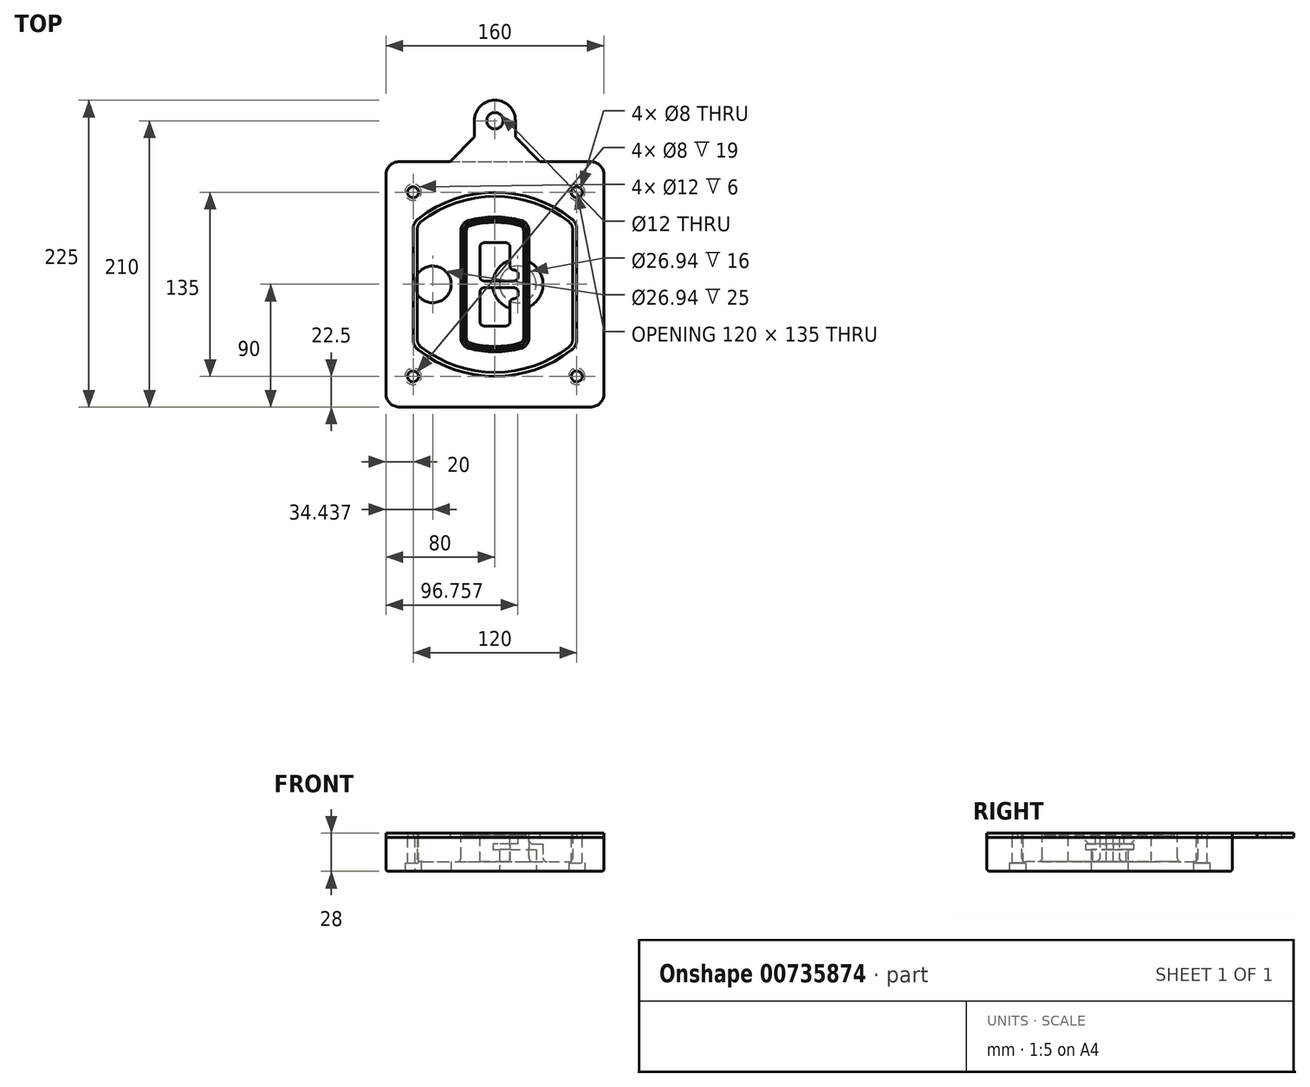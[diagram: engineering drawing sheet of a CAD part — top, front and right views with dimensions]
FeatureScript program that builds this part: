
annotation { "Feature Type Name" : "Feature", "Feature Type Description" : "" }
export const myFeature = defineFeature(function(context is Context, id is Id, definition is map)
    precondition{}
    {
        {
            var Q0;
            Q0=qCreatedBy(makeId("Top.planeOp"),FACE);
            var sketch = newSketch(context, id + "F0", { "sketchPlane" : qUnion([Q0])});
            skPoint(sketch, "E0.rect.middle", {"position": v(0, 0) * mm});
            skLineSegment(sketch, "E1.bottom", {"start": v(-70, -90) * mm, "end": v(70, -90) * mm});
            skLineSegment(sketch, "E1.top", {"start": v(-70, 90) * mm, "end": v(70, 90) * mm});
            skLineSegment(sketch, "E1.left", {"start": v(-80, -80) * mm, "end": v(-80, 80) * mm});
            skLineSegment(sketch, "E1.right", {"start": v(80, -80) * mm, "end": v(80, 80) * mm});
            skLineSegment(sketch, "E2", {"start": v(-80, 90) * mm, "end": v(80, -90) * mm, "construction": true});
            skLineSegment(sketch, "E3", {"start": v(80, 90) * mm, "end": v(-80, -90) * mm, "construction": true});
            skCircle(sketch, "E4", {"center": v(-60, 67.5) * mm, "radius": 4 * mm});
            skCircle(sketch, "E5", {"center": v(60, 67.5) * mm, "radius": 4 * mm});
            skCircle(sketch, "E6", {"center": v(60, -67.5) * mm, "radius": 4 * mm});
            skCircle(sketch, "E7", {"center": v(-60, -67.5) * mm, "radius": 4 * mm});
            skLineSegment(sketch, "E8", {"start": v(-60, 67.5) * mm, "end": v(60, 67.5) * mm, "construction": true});
            skLineSegment(sketch, "E9", {"start": v(60, 67.5) * mm, "end": v(60, -67.5) * mm, "construction": true});
            skLineSegment(sketch, "E10", {"start": v(60, -67.5) * mm, "end": v(-60, -67.5) * mm, "construction": true});
            skLineSegment(sketch, "E11", {"start": v(-60, -67.5) * mm, "end": v(-60, 67.5) * mm, "construction": true});
            skLineSegment(sketch, "E12", {"start": v(-60, 40.3) * mm, "end": v(-60, -40.3) * mm});
            skLineSegment(sketch, "E13", {"start": v(60, 40.3) * mm, "end": v(60, -40.3) * mm});
            skArc(sketch, "E14", {"start": v(56.15, 48.18) * mm, "mid": v(0, 67.5) * mm, "end": v(-56.15, 48.18) * mm});
            skArc(sketch, "E15", {"start": v(-56.15, -48.18) * mm, "mid": v(0, -67.5) * mm, "end": v(56.15, -48.18) * mm});
            skLineSegment(sketch, "E16", {"start": v(-60, 0) * mm, "end": v(60, 0) * mm, "construction": true});
            skPoint(sketch, "E17.visualSharp", {"position": v(-60, -45) * mm});
            skArc(sketch, "E17.filletArc", {"start": v(-60, -40.3) * mm, "mid": v(-58.99, -44.68) * mm, "end": v(-56.15, -48.18) * mm});
            skPoint(sketch, "E18.visualSharp", {"position": v(-60, 45) * mm});
            skArc(sketch, "E18.filletArc", {"start": v(-56.15, 48.18) * mm, "mid": v(-58.99, 44.68) * mm, "end": v(-60, 40.3) * mm});
            skPoint(sketch, "E19.visualSharp", {"position": v(60, 45) * mm});
            skArc(sketch, "E19.filletArc", {"start": v(60, 40.3) * mm, "mid": v(58.99, 44.68) * mm, "end": v(56.15, 48.18) * mm});
            skPoint(sketch, "E20.visualSharp", {"position": v(60, -45) * mm});
            skArc(sketch, "E20.filletArc", {"start": v(56.15, -48.18) * mm, "mid": v(58.99, -44.68) * mm, "end": v(60, -40.3) * mm});
            skPoint(sketch, "E21.visualSharp", {"position": v(-80, 90) * mm});
            skArc(sketch, "E21.filletArc", {"start": v(-70, 90) * mm, "mid": v(-77.07, 87.07) * mm, "end": v(-80, 80) * mm});
            skPoint(sketch, "E22.visualSharp", {"position": v(80, 90) * mm});
            skArc(sketch, "E22.filletArc", {"start": v(80, 80) * mm, "mid": v(77.07, 87.07) * mm, "end": v(70, 90) * mm});
            skPoint(sketch, "E23.visualSharp", {"position": v(80, -90) * mm});
            skArc(sketch, "E23.filletArc", {"start": v(70, -90) * mm, "mid": v(77.07, -87.07) * mm, "end": v(80, -80) * mm});
            skPoint(sketch, "E24.visualSharp", {"position": v(-80, -90) * mm});
            skArc(sketch, "E24.filletArc", {"start": v(-80, -80) * mm, "mid": v(-77.07, -87.07) * mm, "end": v(-70, -90) * mm});
            skArc(sketch, "E25.0", {"start": v(57, 40.3) * mm, "mid": v(56.3, 43.36) * mm, "end": v(54.3, 45.81) * mm});
            skLineSegment(sketch, "E25.1", {"start": v(57, 40.3) * mm, "end": v(57, -40.3) * mm});
            skArc(sketch, "E25.2", {"start": v(54.3, -45.81) * mm, "mid": v(56.3, -43.36) * mm, "end": v(57, -40.3) * mm});
            skArc(sketch, "E25.3", {"start": v(-54.3, -45.81) * mm, "mid": v(0, -64.5) * mm, "end": v(54.3, -45.81) * mm});
            skArc(sketch, "E25.4", {"start": v(-57, -40.3) * mm, "mid": v(-56.3, -43.36) * mm, "end": v(-54.3, -45.81) * mm});
            skArc(sketch, "E25.5", {"start": v(54.3, 45.81) * mm, "mid": v(0, 64.5) * mm, "end": v(-54.3, 45.81) * mm});
            skLineSegment(sketch, "E25.6", {"start": v(-57, 40.3) * mm, "end": v(-57, -40.3) * mm});
            skArc(sketch, "E25.7", {"start": v(-54.3, 45.81) * mm, "mid": v(-56.3, 43.36) * mm, "end": v(-57, 40.3) * mm});
            skArc(sketch, "E26.0", {"start": v(-58.62, 51.33) * mm, "mid": v(-62.58, 46.43) * mm, "end": v(-64, 40.3) * mm});
            skArc(sketch, "E26.1", {"start": v(58.62, 51.33) * mm, "mid": v(0, 71.5) * mm, "end": v(-58.62, 51.33) * mm});
            skArc(sketch, "E26.2", {"start": v(64, 40.3) * mm, "mid": v(62.58, 46.43) * mm, "end": v(58.62, 51.33) * mm});
            skLineSegment(sketch, "E26.3", {"start": v(64, 40.3) * mm, "end": v(64, -40.3) * mm});
            skArc(sketch, "E26.4", {"start": v(58.62, -51.33) * mm, "mid": v(62.58, -46.43) * mm, "end": v(64, -40.3) * mm});
            skLineSegment(sketch, "E26.5", {"start": v(-64, 40.3) * mm, "end": v(-64, -40.3) * mm});
            skArc(sketch, "E26.6", {"start": v(-58.62, -51.33) * mm, "mid": v(0, -71.5) * mm, "end": v(58.62, -51.33) * mm});
            skArc(sketch, "E26.7", {"start": v(-64, -40.3) * mm, "mid": v(-62.58, -46.43) * mm, "end": v(-58.62, -51.33) * mm});
            skSolve(sketch);
        }
        {
            var Q0;
            Q0=makeQuery(id+"F0.imprint","IMPRINT",FACE,{"disambiguationData":[TD([[makeQuery(id+"F0.imprint","IMPRINT",EDGE,{"derivedFrom":sQuery(id+"F0.wireOp",EDGE,"E1.bottom")}),1.0]])]});
            var Q1;
            Q1=makeQuery(id+"F0.imprint","IMPRINT",FACE,{"disambiguationData":[TD([[makeQuery(id+"F0.imprint","IMPRINT",EDGE,{"derivedFrom":sQuery(id+"F0.wireOp",EDGE,"E12")}),1.0]])]});
            var Q2;
            Q2=makeQuery(id+"F0.imprint","IMPRINT",FACE,{"disambiguationData":[TD([[makeQuery(id+"F0.imprint","IMPRINT",EDGE,{"derivedFrom":sQuery(id+"F0.wireOp",EDGE,"E25.0")}),1.0]])]});
            var Q3;
            Q3=makeQuery(id+"F0.imprint","IMPRINT",FACE,{"disambiguationData":[TD([[makeQuery(id+"F0.imprint","IMPRINT",EDGE,{"derivedFrom":sQuery(id+"F0.wireOp",EDGE,"E12")}),-1.0]])]});
            extrude(context, id + "F1", {"entities" : qUnion([Q0, Q1, Q2, Q3]), "oppositeDirection" : true, "depth" : 25 * mm});
        }
        {
            var Q0;
            Q0=makeQuery(id+"F0.imprint","IMPRINT",FACE,{"disambiguationData":[TD([[makeQuery(id+"F0.imprint","IMPRINT",EDGE,{"derivedFrom":sQuery(id+"F0.wireOp",EDGE,"E12")}),1.0]])]});
            extrude(context, id + "F2", {"entities" : qUnion([Q0]), "operationType" : NewBodyOperationType.ADD, "depth" : 3 * mm});
        }
        {
            var Q0;
            Q0=makeQuery(id+"F0.imprint","IMPRINT",FACE,{"disambiguationData":[TD([[makeQuery(id+"F0.imprint","IMPRINT",EDGE,{"derivedFrom":sQuery(id+"F0.wireOp",EDGE,"E25.0")}),1.0]])]});
            extrude(context, id + "F3", {"entities" : qUnion([Q0]), "operationType" : NewBodyOperationType.REMOVE, "oppositeDirection" : true, "depth" : 18 * mm});
        }
        {
            var Q0;
            Q0=makeQuery(id+"F2.opExtrude","CAP_FACE",FACE,{"disambiguationData":[OSD([sQuery(id+"F0.wireOp",EDGE,"E12"),sQuery(id+"F0.wireOp",EDGE,"E13"),sQuery(id+"F0.wireOp",EDGE,"E14"),sQuery(id+"F0.wireOp",EDGE,"E15"),sQuery(id+"F0.wireOp",EDGE,"E17.filletArc"),sQuery(id+"F0.wireOp",EDGE,"E18.filletArc"),sQuery(id+"F0.wireOp",EDGE,"E19.filletArc"),sQuery(id+"F0.wireOp",EDGE,"E20.filletArc"),sQuery(id+"F0.wireOp",EDGE,"E25.0"),sQuery(id+"F0.wireOp",EDGE,"E25.1"),sQuery(id+"F0.wireOp",EDGE,"E25.2"),sQuery(id+"F0.wireOp",EDGE,"E25.3"),sQuery(id+"F0.wireOp",EDGE,"E25.4"),sQuery(id+"F0.wireOp",EDGE,"E25.5"),sQuery(id+"F0.wireOp",EDGE,"E25.6"),sQuery(id+"F0.wireOp",EDGE,"E25.7")])],"isStart":false});
            var sketch = newSketch(context, id + "F4", { "sketchPlane" : qUnion([Q0])});
            skArc(sketch, "E27.0", {"start": v(-19.08, -46.97) * mm, "mid": v(0, -49.5) * mm, "end": v(19.08, -46.97) * mm});
            skArc(sketch, "E28.0", {"start": v(19.08, 46.97) * mm, "mid": v(0, 49.5) * mm, "end": v(-19.08, 46.97) * mm});
            skLineSegment(sketch, "E29", {"start": v(-25, 39.25) * mm, "end": v(-25, -39.25) * mm});
            skLineSegment(sketch, "E30", {"start": v(25, 39.25) * mm, "end": v(25, -39.25) * mm});
            skLineSegment(sketch, "E31", {"start": v(-25, 45.1) * mm, "end": v(25, 45.1) * mm, "construction": true});
            skLineSegment(sketch, "E32", {"start": v(-25, -45.1) * mm, "end": v(25, -45.1) * mm, "construction": true});
            skPoint(sketch, "E33.visualSharp", {"position": v(-25, 45.1) * mm});
            skArc(sketch, "E33.filletArc", {"start": v(-19.08, 46.97) * mm, "mid": v(-23.35, 44.11) * mm, "end": v(-25, 39.25) * mm});
            skPoint(sketch, "E34.visualSharp", {"position": v(25, 45.1) * mm});
            skArc(sketch, "E34.filletArc", {"start": v(25, 39.25) * mm, "mid": v(23.35, 44.11) * mm, "end": v(19.08, 46.97) * mm});
            skPoint(sketch, "E35.visualSharp", {"position": v(25, -45.1) * mm});
            skArc(sketch, "E35.filletArc", {"start": v(19.08, -46.97) * mm, "mid": v(23.35, -44.11) * mm, "end": v(25, -39.25) * mm});
            skPoint(sketch, "E36.visualSharp", {"position": v(-25, -45.1) * mm});
            skArc(sketch, "E36.filletArc", {"start": v(-25, -39.25) * mm, "mid": v(-23.35, -44.11) * mm, "end": v(-19.08, -46.97) * mm});
            skArc(sketch, "E37.0", {"start": v(54.3, 45.81) * mm, "mid": v(0, 64.5) * mm, "end": v(-54.3, 45.81) * mm});
            skArc(sketch, "E37.1", {"start": v(-54.3, 45.81) * mm, "mid": v(-56.3, 43.36) * mm, "end": v(-57, 40.3) * mm});
            skLineSegment(sketch, "E37.2", {"start": v(-57, 40.3) * mm, "end": v(-57, -40.3) * mm});
            skArc(sketch, "E37.3", {"start": v(-57, -40.3) * mm, "mid": v(-56.3, -43.36) * mm, "end": v(-54.3, -45.81) * mm});
            skArc(sketch, "E37.4", {"start": v(-54.3, -45.81) * mm, "mid": v(0, -64.5) * mm, "end": v(54.3, -45.81) * mm});
            skArc(sketch, "E37.5", {"start": v(54.3, -45.81) * mm, "mid": v(56.3, -43.36) * mm, "end": v(57, -40.3) * mm});
            skLineSegment(sketch, "E37.6", {"start": v(57, 40.3) * mm, "end": v(57, -40.3) * mm});
            skArc(sketch, "E37.7", {"start": v(57, 40.3) * mm, "mid": v(56.3, 43.36) * mm, "end": v(54.3, 45.81) * mm});
            skLineSegment(sketch, "E38.0", {"start": v(23, 39.25) * mm, "end": v(23, -39.25) * mm});
            skArc(sketch, "E38.1", {"start": v(18.56, -45.04) * mm, "mid": v(21.76, -42.9) * mm, "end": v(23, -39.25) * mm});
            skArc(sketch, "E38.2", {"start": v(-18.56, -45.04) * mm, "mid": v(0, -47.5) * mm, "end": v(18.56, -45.04) * mm});
            skArc(sketch, "E38.3", {"start": v(-23, -39.25) * mm, "mid": v(-21.76, -42.9) * mm, "end": v(-18.56, -45.04) * mm});
            skLineSegment(sketch, "E38.4", {"start": v(-23, 39.25) * mm, "end": v(-23, -39.25) * mm});
            skArc(sketch, "E38.5", {"start": v(23, 39.25) * mm, "mid": v(21.76, 42.9) * mm, "end": v(18.56, 45.04) * mm});
            skArc(sketch, "E38.6", {"start": v(-18.56, 45.04) * mm, "mid": v(-21.76, 42.9) * mm, "end": v(-23, 39.25) * mm});
            skArc(sketch, "E38.7", {"start": v(18.56, 45.04) * mm, "mid": v(0, 47.5) * mm, "end": v(-18.56, 45.04) * mm});
            skArc(sketch, "E39.0", {"start": v(21, 39.25) * mm, "mid": v(20.18, 41.68) * mm, "end": v(18.04, 43.1) * mm});
            skLineSegment(sketch, "E39.1", {"start": v(21, 39.25) * mm, "end": v(21, -39.25) * mm});
            skArc(sketch, "E39.2", {"start": v(18.04, -43.1) * mm, "mid": v(20.18, -41.68) * mm, "end": v(21, -39.25) * mm});
            skArc(sketch, "E39.3", {"start": v(-18.04, -43.1) * mm, "mid": v(0, -45.5) * mm, "end": v(18.04, -43.1) * mm});
            skArc(sketch, "E39.4", {"start": v(-21, -39.25) * mm, "mid": v(-20.18, -41.68) * mm, "end": v(-18.04, -43.1) * mm});
            skArc(sketch, "E39.5", {"start": v(18.04, 43.1) * mm, "mid": v(0, 45.5) * mm, "end": v(-18.04, 43.1) * mm});
            skLineSegment(sketch, "E39.6", {"start": v(-21, 39.25) * mm, "end": v(-21, -39.25) * mm});
            skArc(sketch, "E39.7", {"start": v(-18.04, 43.1) * mm, "mid": v(-20.18, 41.68) * mm, "end": v(-21, 39.25) * mm});
            skLineSegment(sketch, "E40", {"start": v(-25, 0) * mm, "end": v(25, 0) * mm, "construction": true});
            skLineSegment(sketch, "E41", {"start": v(-11, 5.5) * mm, "end": v(-11, 27.5) * mm});
            skLineSegment(sketch, "E42", {"start": v(-8, 30.5) * mm, "end": v(8, 30.5) * mm});
            skLineSegment(sketch, "E43", {"start": v(11, 27.5) * mm, "end": v(11, 13.5) * mm});
            skLineSegment(sketch, "E44", {"start": v(14, 10.5) * mm, "end": v(14, 10.5) * mm});
            skLineSegment(sketch, "E45", {"start": v(17, 7.5) * mm, "end": v(17, 5.5) * mm});
            skLineSegment(sketch, "E46", {"start": v(14, 2.5) * mm, "end": v(-8, 2.5) * mm});
            skPoint(sketch, "E47.visualSharp", {"position": v(-11, 30.5) * mm});
            skArc(sketch, "E47.filletArc", {"start": v(-8, 30.5) * mm, "mid": v(-10.12, 29.62) * mm, "end": v(-11, 27.5) * mm});
            skPoint(sketch, "E48.visualSharp", {"position": v(11, 30.5) * mm});
            skArc(sketch, "E48.filletArc", {"start": v(11, 27.5) * mm, "mid": v(10.12, 29.62) * mm, "end": v(8, 30.5) * mm});
            skPoint(sketch, "E49.visualSharp", {"position": v(11, 10.5) * mm});
            skArc(sketch, "E49.filletArc", {"start": v(11, 13.5) * mm, "mid": v(11.88, 11.38) * mm, "end": v(14, 10.5) * mm});
            skPoint(sketch, "E50.visualSharp", {"position": v(17, 10.5) * mm});
            skArc(sketch, "E50.filletArc", {"start": v(17, 7.5) * mm, "mid": v(16.12, 9.62) * mm, "end": v(14, 10.5) * mm});
            skPoint(sketch, "E51.visualSharp", {"position": v(17, 2.5) * mm});
            skArc(sketch, "E51.filletArc", {"start": v(14, 2.5) * mm, "mid": v(16.12, 3.38) * mm, "end": v(17, 5.5) * mm});
            skPoint(sketch, "E52.visualSharp", {"position": v(-11, 2.5) * mm});
            skArc(sketch, "E52.filletArc", {"start": v(-11, 5.5) * mm, "mid": v(-10.12, 3.38) * mm, "end": v(-8, 2.5) * mm});
            skLineSegment(sketch, "E53.0.MirrorCS", {"start": v(14, -2.5) * mm, "end": v(-8, -2.5) * mm});
            skArc(sketch, "E54.0.MirrorCS", {"start": v(-11, -5.5) * mm, "mid": v(-10.12, -3.38) * mm, "end": v(-8, -2.5) * mm});
            skLineSegment(sketch, "E55.0.MirrorCS", {"start": v(-11, -5.5) * mm, "end": v(-11, -27.5) * mm});
            skArc(sketch, "E56.0.MirrorCS", {"start": v(-8, -30.5) * mm, "mid": v(-10.12, -29.62) * mm, "end": v(-11, -27.5) * mm});
            skLineSegment(sketch, "E57.0.MirrorCS", {"start": v(-8, -30.5) * mm, "end": v(8, -30.5) * mm});
            skArc(sketch, "E58.0.MirrorCS", {"start": v(11, -27.5) * mm, "mid": v(10.12, -29.62) * mm, "end": v(8, -30.5) * mm});
            skLineSegment(sketch, "E59.0.MirrorCS", {"start": v(11, -27.5) * mm, "end": v(11, -13.5) * mm});
            skArc(sketch, "E60.0.MirrorCS", {"start": v(11, -13.5) * mm, "mid": v(11.88, -11.38) * mm, "end": v(14, -10.5) * mm});
            skArc(sketch, "E61.0.MirrorCS", {"start": v(17, -7.5) * mm, "mid": v(16.12, -9.62) * mm, "end": v(14, -10.5) * mm});
            skLineSegment(sketch, "E62.0.MirrorCS", {"start": v(17, -7.5) * mm, "end": v(17, -5.5) * mm});
            skArc(sketch, "E63.0.MirrorCS", {"start": v(14, -2.5) * mm, "mid": v(16.12, -3.38) * mm, "end": v(17, -5.5) * mm});
            skSolve(sketch);
        }
        {
            var Q0;
            Q0=makeQuery(id+"F4.imprint","IMPRINT",FACE,{"disambiguationData":[TD([[makeQuery(id+"F4.imprint","IMPRINT",EDGE,{"derivedFrom":sQuery(id+"F4.wireOp",EDGE,"E27.0")}),1.0]])]});
            var Q1;
            Q1=makeQuery(id+"F4.imprint","IMPRINT",FACE,{"disambiguationData":[TD([[makeQuery(id+"F4.imprint","IMPRINT",EDGE,{"derivedFrom":sQuery(id+"F4.wireOp",EDGE,"E38.0")}),-1.0]])]});
            var Q2;
            Q2=makeQuery(id+"F4.imprint","IMPRINT",FACE,{"disambiguationData":[TD([[makeQuery(id+"F4.imprint","IMPRINT",EDGE,{"derivedFrom":sQuery(id+"F4.wireOp",EDGE,"E39.0")}),1.0]])]});
            extrude(context, id + "F5", {"entities" : qUnion([Q0, Q1, Q2]), "operationType" : NewBodyOperationType.ADD, "endBound" : BoundingType.UP_TO_NEXT, "oppositeDirection" : true, "depth" : 25 * mm});
        }
        {
            var Q0;
            Q0=makeQuery(id+"F4.imprint","IMPRINT",FACE,{"disambiguationData":[TD([[makeQuery(id+"F4.imprint","IMPRINT",EDGE,{"derivedFrom":sQuery(id+"F4.wireOp",EDGE,"E38.0")}),-1.0]])]});
            extrude(context, id + "F6", {"entities" : qUnion([Q0]), "operationType" : NewBodyOperationType.REMOVE, "oppositeDirection" : true, "depth" : 2 * mm});
        }
        {
            var Q0;
            Q0=makeQuery(id+"F1.opExtrude","CAP_FACE",FACE,{"disambiguationData":[OSD([sQuery(id+"F0.wireOp",EDGE,"E1.bottom"),sQuery(id+"F0.wireOp",EDGE,"E1.top"),sQuery(id+"F0.wireOp",EDGE,"E1.left"),sQuery(id+"F0.wireOp",EDGE,"E1.right"),sQuery(id+"F0.wireOp",EDGE,"E4"),sQuery(id+"F0.wireOp",EDGE,"E5"),sQuery(id+"F0.wireOp",EDGE,"E6"),sQuery(id+"F0.wireOp",EDGE,"E7"),sQuery(id+"F0.wireOp",EDGE,"E21.filletArc"),sQuery(id+"F0.wireOp",EDGE,"E22.filletArc"),sQuery(id+"F0.wireOp",EDGE,"E23.filletArc"),sQuery(id+"F0.wireOp",EDGE,"E24.filletArc")])],"isStart":false});
            var sketch = newSketch(context, id + "F7", { "sketchPlane" : qUnion([Q0])});
            skCircle(sketch, "E64", {"center": v(16.76, 0) * mm, "radius": 13.47 * mm});
            skCircle(sketch, "E65", {"center": v(-45.56, 0) * mm, "radius": 13.47 * mm});
            skLineSegment(sketch, "E66", {"start": v(80, 0) * mm, "end": v(-80, 0) * mm});
            skCircle(sketch, "E67", {"center": v(16.76, 0) * mm, "radius": 18.47 * mm});
            skCircle(sketch, "E68", {"center": v(60, -67.5) * mm, "radius": 6 * mm});
            skCircle(sketch, "E69", {"center": v(-60, -67.5) * mm, "radius": 6 * mm});
            skCircle(sketch, "E70", {"center": v(-60, 67.5) * mm, "radius": 6 * mm});
            skCircle(sketch, "E71", {"center": v(60, 67.5) * mm, "radius": 6 * mm});
            skSolve(sketch);
        }
        {
            var Q0;
            {var subQ1=sQuery(id+"F7.wireOp",EDGE,"E66");var subQ4=sQuery(id+"F7.wireOp",EDGE,"E64");var subQ6=makeQuery(id+"F7.imprint","INTERSECT",VERTEX,{"disambiguationData":[OD(0.0)],"derivedFrom":[subQ4,subQ1]});Q0=makeQuery(id+"F7.imprint","IMPRINT",FACE,{"disambiguationData":[TD([[makeQuery(id+"F7.imprint","IMPRINT",EDGE,{"disambiguationData":[TD([[subQ6,-1.0]])],"derivedFrom":subQ4}),-1.0]])]});}
            var Q1;
            {var subQ0=sQuery(id+"F7.wireOp",EDGE,"E66");var subQ1=sQuery(id+"F7.wireOp",EDGE,"E64");var subQ3=makeQuery(id+"F7.imprint","INTERSECT",VERTEX,{"disambiguationData":[OD(0.0)],"derivedFrom":[subQ1,subQ0]});Q1=makeQuery(id+"F7.imprint","IMPRINT",FACE,{"disambiguationData":[TD([[makeQuery(id+"F7.imprint","IMPRINT",EDGE,{"disambiguationData":[TD([[subQ3,-1.0]])],"derivedFrom":subQ1}),1.0]])]});}
            var Q2;
            {var subQ0=sQuery(id+"F7.wireOp",EDGE,"E66");var subQ1=sQuery(id+"F7.wireOp",EDGE,"E64");var subQ3=makeQuery(id+"F7.imprint","INTERSECT",VERTEX,{"disambiguationData":[OD(0.0)],"derivedFrom":[subQ1,subQ0]});Q2=makeQuery(id+"F7.imprint","IMPRINT",FACE,{"disambiguationData":[TD([[makeQuery(id+"F7.imprint","IMPRINT",EDGE,{"disambiguationData":[TD([[subQ3,1.0]])],"derivedFrom":subQ1}),1.0]])]});}
            var Q3;
            {var subQ1=sQuery(id+"F7.wireOp",EDGE,"E66");var subQ4=sQuery(id+"F7.wireOp",EDGE,"E64");var subQ6=makeQuery(id+"F7.imprint","INTERSECT",VERTEX,{"disambiguationData":[OD(0.0)],"derivedFrom":[subQ4,subQ1]});Q3=makeQuery(id+"F7.imprint","IMPRINT",FACE,{"disambiguationData":[TD([[makeQuery(id+"F7.imprint","IMPRINT",EDGE,{"disambiguationData":[TD([[subQ6,1.0]])],"derivedFrom":subQ4}),-1.0]])]});}
            extrude(context, id + "F8", {"entities" : qUnion([Q0, Q1, Q2, Q3]), "operationType" : NewBodyOperationType.ADD, "oppositeDirection" : true, "depth" : 20 * mm});
        }
        {
            var Q0;
            {var subQ0=sQuery(id+"F7.wireOp",EDGE,"E66");var subQ1=sQuery(id+"F7.wireOp",EDGE,"E64");var subQ3=makeQuery(id+"F7.imprint","INTERSECT",VERTEX,{"disambiguationData":[OD(0.0)],"derivedFrom":[subQ1,subQ0]});Q0=makeQuery(id+"F7.imprint","IMPRINT",FACE,{"disambiguationData":[TD([[makeQuery(id+"F7.imprint","IMPRINT",EDGE,{"disambiguationData":[TD([[subQ3,-1.0]])],"derivedFrom":subQ1}),1.0]])]});}
            var Q1;
            {var subQ0=sQuery(id+"F7.wireOp",EDGE,"E66");var subQ1=sQuery(id+"F7.wireOp",EDGE,"E64");var subQ3=makeQuery(id+"F7.imprint","INTERSECT",VERTEX,{"disambiguationData":[OD(0.0)],"derivedFrom":[subQ1,subQ0]});Q1=makeQuery(id+"F7.imprint","IMPRINT",FACE,{"disambiguationData":[TD([[makeQuery(id+"F7.imprint","IMPRINT",EDGE,{"disambiguationData":[TD([[subQ3,1.0]])],"derivedFrom":subQ1}),1.0]])]});}
            extrude(context, id + "F9", {"entities" : qUnion([Q0, Q1]), "operationType" : NewBodyOperationType.REMOVE, "oppositeDirection" : true, "depth" : 16 * mm});
        }
        {
            var Q0;
            {var subQ0=sQuery(id+"F7.wireOp",EDGE,"E66");var subQ1=sQuery(id+"F7.wireOp",EDGE,"E65");var subQ3=makeQuery(id+"F7.imprint","INTERSECT",VERTEX,{"disambiguationData":[OD(0.0)],"derivedFrom":[subQ1,subQ0]});Q0=makeQuery(id+"F7.imprint","IMPRINT",FACE,{"disambiguationData":[TD([[makeQuery(id+"F7.imprint","IMPRINT",EDGE,{"disambiguationData":[TD([[subQ3,-1.0]])],"derivedFrom":subQ1}),1.0]])]});}
            var Q1;
            {var subQ0=sQuery(id+"F7.wireOp",EDGE,"E66");var subQ1=sQuery(id+"F7.wireOp",EDGE,"E65");var subQ3=makeQuery(id+"F7.imprint","INTERSECT",VERTEX,{"disambiguationData":[OD(0.0)],"derivedFrom":[subQ1,subQ0]});Q1=makeQuery(id+"F7.imprint","IMPRINT",FACE,{"disambiguationData":[TD([[makeQuery(id+"F7.imprint","IMPRINT",EDGE,{"disambiguationData":[TD([[subQ3,1.0]])],"derivedFrom":subQ1}),1.0]])]});}
            extrude(context, id + "F10", {"entities" : qUnion([Q0, Q1]), "operationType" : NewBodyOperationType.REMOVE, "oppositeDirection" : true, "depth" : 25 * mm});
        }
        {
            var Q0;
            Q0=makeQuery(id+"F7.imprint","IMPRINT",FACE,{"disambiguationData":[TD([[makeQuery(id+"F7.imprint","IMPRINT",EDGE,{"derivedFrom":sQuery(id+"F7.wireOp",EDGE,"E68")}),1.0]])]});
            var Q1;
            Q1=makeQuery(id+"F7.imprint","IMPRINT",FACE,{"disambiguationData":[TD([[makeQuery(id+"F7.imprint","IMPRINT",EDGE,{"derivedFrom":makeQuery(id+"F1.opExtrude","CAP_EDGE",EDGE,{"disambiguationData":[OSD([sQuery(id+"F0.wireOp",EDGE,"E5")])],"isStart":false})}),-1.0]])]});
            var Q2;
            Q2=makeQuery(id+"F7.imprint","IMPRINT",FACE,{"disambiguationData":[TD([[makeQuery(id+"F7.imprint","IMPRINT",EDGE,{"derivedFrom":sQuery(id+"F7.wireOp",EDGE,"E69")}),1.0]])]});
            var Q3;
            Q3=makeQuery(id+"F7.imprint","IMPRINT",FACE,{"disambiguationData":[TD([[makeQuery(id+"F7.imprint","IMPRINT",EDGE,{"derivedFrom":makeQuery(id+"F1.opExtrude","CAP_EDGE",EDGE,{"disambiguationData":[OSD([sQuery(id+"F0.wireOp",EDGE,"E4")])],"isStart":false})}),-1.0]])]});
            var Q4;
            Q4=makeQuery(id+"F7.imprint","IMPRINT",FACE,{"disambiguationData":[TD([[makeQuery(id+"F7.imprint","IMPRINT",EDGE,{"derivedFrom":sQuery(id+"F7.wireOp",EDGE,"E70")}),1.0]])]});
            var Q5;
            Q5=makeQuery(id+"F7.imprint","IMPRINT",FACE,{"disambiguationData":[TD([[makeQuery(id+"F7.imprint","IMPRINT",EDGE,{"derivedFrom":makeQuery(id+"F1.opExtrude","CAP_EDGE",EDGE,{"disambiguationData":[OSD([sQuery(id+"F0.wireOp",EDGE,"E7")])],"isStart":false})}),-1.0]])]});
            var Q6;
            Q6=makeQuery(id+"F7.imprint","IMPRINT",FACE,{"disambiguationData":[TD([[makeQuery(id+"F7.imprint","IMPRINT",EDGE,{"derivedFrom":sQuery(id+"F7.wireOp",EDGE,"E71")}),1.0]])]});
            var Q7;
            Q7=makeQuery(id+"F7.imprint","IMPRINT",FACE,{"disambiguationData":[TD([[makeQuery(id+"F7.imprint","IMPRINT",EDGE,{"derivedFrom":makeQuery(id+"F1.opExtrude","CAP_EDGE",EDGE,{"disambiguationData":[OSD([sQuery(id+"F0.wireOp",EDGE,"E6")])],"isStart":false})}),-1.0]])]});
            extrude(context, id + "F11", {"entities" : qUnion([Q0, Q1, Q2, Q3, Q4, Q5, Q6, Q7]), "operationType" : NewBodyOperationType.REMOVE, "oppositeDirection" : true, "depth" : 6 * mm});
        }
        {
            var Q0;
            Q0=makeQuery(id+"F9.boolean.opBoolean","COPY",FACE,{"derivedFrom":makeQuery(id+"F9.opExtrude","CAP_FACE",FACE,{"disambiguationData":[OSD([sQuery(id+"F7.wireOp",EDGE,"E64")])],"isStart":false})});
            var sketch = newSketch(context, id + "F12", { "sketchPlane" : qUnion([Q0])});
            skArc(sketch, "E72.0", {"start": v(11, 17.55) * mm, "mid": v(2.57, 11.82) * mm, "end": v(-1.54, 2.5) * mm});
            skArc(sketch, "E72.1", {"start": v(-1.54, -2.5) * mm, "mid": v(2.57, -11.82) * mm, "end": v(11, -17.55) * mm});
            skLineSegment(sketch, "E73", {"start": v(-1.54, -2.5) * mm, "end": v(14, -2.5) * mm});
            skLineSegment(sketch, "E74.0", {"start": v(14, 2.5) * mm, "end": v(-1.54, 2.5) * mm});
            skArc(sketch, "E74.1", {"start": v(14, 2.5) * mm, "mid": v(16.12, 3.38) * mm, "end": v(17, 5.5) * mm});
            skLineSegment(sketch, "E74.2", {"start": v(17, 7.5) * mm, "end": v(17, 5.5) * mm});
            skArc(sketch, "E74.3", {"start": v(17, 7.5) * mm, "mid": v(16.12, 9.62) * mm, "end": v(14, 10.5) * mm});
            skArc(sketch, "E74.4", {"start": v(11, 13.5) * mm, "mid": v(11.88, 11.38) * mm, "end": v(14, 10.5) * mm});
            skLineSegment(sketch, "E74.5", {"start": v(11, 17.55) * mm, "end": v(11, 13.5) * mm});
            skLineSegment(sketch, "E74.7", {"start": v(14, -2.5) * mm, "end": v(-1.54, -2.5) * mm});
            skArc(sketch, "E74.8", {"start": v(14, -2.5) * mm, "mid": v(16.12, -3.38) * mm, "end": v(17, -5.5) * mm});
            skLineSegment(sketch, "E74.9", {"start": v(17, -7.5) * mm, "end": v(17, -5.5) * mm});
            skArc(sketch, "E74.10", {"start": v(17, -7.5) * mm, "mid": v(16.12, -9.62) * mm, "end": v(14, -10.5) * mm});
            skArc(sketch, "E74.11", {"start": v(11, -13.5) * mm, "mid": v(11.88, -11.38) * mm, "end": v(14, -10.5) * mm});
            skLineSegment(sketch, "E74.12", {"start": v(11, -17.55) * mm, "end": v(11, -13.5) * mm});
            skPoint(sketch, "E75.orphan", {"position": v(11, -27.5) * mm});
            skPoint(sketch, "E76.orphan", {"position": v(-8, -2.5) * mm});
            skPoint(sketch, "E77.orphan", {"position": v(-8, 2.5) * mm});
            skPoint(sketch, "E78.orphan", {"position": v(11, 27.5) * mm});
            skSolve(sketch);
        }
        {
            var Q0;
            {var subQ7=sQuery(id+"F12.wireOp",EDGE,"E72.0");var subQ14=sQuery(id+"F12.wireOp",EDGE,"E72.1");var subQ16=sQuery(id+"F12.wireOp",EDGE,"E74.1");var subQ18=sQuery(id+"F12.wireOp",EDGE,"E74.8");Q0=qUnion([makeQuery(id+"F12.imprint","IMPRINT",FACE,{"disambiguationData":[TD([[makeQuery(id+"F12.imprint","IMPRINT",EDGE,{"derivedFrom":subQ7}),1.0]])]}),makeQuery(id+"F12.imprint","IMPRINT",FACE,{"disambiguationData":[TD([[makeQuery(id+"F12.imprint","IMPRINT",EDGE,{"derivedFrom":subQ14}),1.0]])]}),makeQuery(id+"F12.imprint","IMPRINT",FACE,{"disambiguationData":[TD([[makeQuery(id+"F12.imprint","IMPRINT",EDGE,{"derivedFrom":subQ16}),1.0]])]}),makeQuery(id+"F12.imprint","IMPRINT",FACE,{"disambiguationData":[TD([[makeQuery(id+"F12.imprint","IMPRINT",EDGE,{"derivedFrom":subQ18}),-1.0]])]})]);}
            var Q1;
            Q1=makeQuery(id+"F5.boolean.opBoolean","SPLIT",FACE,{"disambiguationData":[TD([makeQuery(id+"F5.opExtrude","SWEPT_FACE",FACE,{"disambiguationData":[OSD([sQuery(id+"F4.wireOp",EDGE,"E41")])]})])],"derivedFrom":makeQuery(id+"F3.boolean.opBoolean","COPY",FACE,{"derivedFrom":makeQuery(id+"F3.opExtrude","CAP_FACE",FACE,{"disambiguationData":[OSD([sQuery(id+"F0.wireOp",EDGE,"E25.0"),sQuery(id+"F0.wireOp",EDGE,"E25.1"),sQuery(id+"F0.wireOp",EDGE,"E25.2"),sQuery(id+"F0.wireOp",EDGE,"E25.3"),sQuery(id+"F0.wireOp",EDGE,"E25.4"),sQuery(id+"F0.wireOp",EDGE,"E25.5"),sQuery(id+"F0.wireOp",EDGE,"E25.6"),sQuery(id+"F0.wireOp",EDGE,"E25.7")])],"isStart":false})})});
            extrude(context, id + "F13", {"entities" : qUnion([Q0]), "operationType" : NewBodyOperationType.REMOVE, "endBound" : BoundingType.UP_TO_SURFACE, "endBoundEntityFace" : qUnion([Q1]), "depth" : 25 * mm});
        }
        {
            var Q0;
            Q0=makeQuery(id+"F3.boolean.opBoolean","COPY",EDGE,{"derivedFrom":makeQuery(id+"F3.opExtrude","CAP_EDGE",EDGE,{"disambiguationData":[OSD([sQuery(id+"F0.wireOp",EDGE,"E25.6")])],"isStart":false})});
            var Q1;
            Q1=makeQuery(id+"F8.boolean.opBoolean","INTERSECT",EDGE,{"derivedFrom":[makeQuery(id+"F5.opExtrude","SWEPT_FACE",FACE,{"disambiguationData":[OSD([sQuery(id+"F4.wireOp",EDGE,"E30")])]}),makeQuery(id+"F8.opExtrude","CAP_FACE",FACE,{"disambiguationData":[OSD([sQuery(id+"F7.wireOp",EDGE,"E67")])],"isStart":false})]});
            var Q2;
            Q2=makeQuery(id+"F8.boolean.opBoolean","INTERSECT",EDGE,{"disambiguationData":[OD(1.0)],"derivedFrom":[makeQuery(id+"F5.opExtrude","SWEPT_FACE",FACE,{"disambiguationData":[OSD([sQuery(id+"F4.wireOp",EDGE,"E30")])]}),makeQuery(id+"F8.opExtrude","SWEPT_FACE",FACE,{"disambiguationData":[OSD([sQuery(id+"F7.wireOp",EDGE,"E67")])]})]});
            var Q3;
            {var subQ0=sQuery(id+"F4.wireOp",EDGE,"E30");Q3=makeQuery(id+"F8.boolean.opBoolean","SPLIT",EDGE,{"disambiguationData":[TD([makeQuery(id+"F5.opExtrude","SWEPT_FACE",FACE,{"disambiguationData":[OSD([sQuery(id+"F4.wireOp",EDGE,"E35.filletArc")])]})])],"derivedFrom":makeQuery(id+"F5.opExtrude","CAP_EDGE",EDGE,{"disambiguationData":[OSD([subQ0])],"isStart":false})});}
            var Q4;
            {var subQ0=sQuery(id+"F0.wireOp",EDGE,"E25.7");var subQ1=sQuery(id+"F0.wireOp",EDGE,"E25.1");var subQ2=sQuery(id+"F0.wireOp",EDGE,"E25.6");var subQ3=sQuery(id+"F0.wireOp",EDGE,"E25.5");var subQ4=sQuery(id+"F0.wireOp",EDGE,"E25.4");var subQ5=sQuery(id+"F0.wireOp",EDGE,"E25.0");var subQ6=sQuery(id+"F0.wireOp",EDGE,"E25.2");var subQ7=sQuery(id+"F0.wireOp",EDGE,"E25.3");Q4=makeQuery(id+"F8.boolean.opBoolean","INTERSECT",EDGE,{"derivedFrom":[makeQuery(id+"F5.boolean.opBoolean","SPLIT",FACE,{"disambiguationData":[TD([makeQuery(id+"F2.opExtrude","SWEPT_FACE",FACE,{"disambiguationData":[OSD([subQ5])]})])],"derivedFrom":makeQuery(id+"F3.boolean.opBoolean","COPY",FACE,{"derivedFrom":makeQuery(id+"F3.opExtrude","CAP_FACE",FACE,{"disambiguationData":[OSD([subQ5,subQ1,subQ6,subQ7,subQ4,subQ3,subQ2,subQ0])],"isStart":false})})}),makeQuery(id+"F8.opExtrude","SWEPT_FACE",FACE,{"disambiguationData":[OSD([sQuery(id+"F7.wireOp",EDGE,"E67")])]})]});}
            var Q5;
            Q5=makeQuery(id+"F8.boolean.opBoolean","INTERSECT",EDGE,{"disambiguationData":[OD(0.0)],"derivedFrom":[makeQuery(id+"F5.opExtrude","SWEPT_FACE",FACE,{"disambiguationData":[OSD([sQuery(id+"F4.wireOp",EDGE,"E30")])]}),makeQuery(id+"F8.opExtrude","SWEPT_FACE",FACE,{"disambiguationData":[OSD([sQuery(id+"F7.wireOp",EDGE,"E67")])]})]});
            fillet(context, id + "F14", {"entities" : qUnion([Q0, Q1, Q2, Q3, Q4, Q5]), "radius" : 3 * mm, "tangentPropagation" : true, "allowEdgeOverflow" : false});
        }
        {
            var Q0;
            Q0=makeQuery(id+"F1.opExtrude","CAP_EDGE",EDGE,{"disambiguationData":[OSD([sQuery(id+"F0.wireOp",EDGE,"E1.bottom")])],"isStart":false});
            fillet(context, id + "F15", {"entities" : qUnion([Q0]), "radius" : 2 * mm, "tangentPropagation" : true, "allowEdgeOverflow" : false});
        }
        {
            var Q0;
            {var subQ0=sQuery(id+"F0.wireOp",EDGE,"E21.filletArc");var subQ1=sQuery(id+"F0.wireOp",EDGE,"E7");var subQ2=sQuery(id+"F0.wireOp",EDGE,"E6");var subQ3=sQuery(id+"F0.wireOp",EDGE,"E5");var subQ4=sQuery(id+"F0.wireOp",EDGE,"E4");var subQ5=sQuery(id+"F0.wireOp",EDGE,"E22.filletArc");var subQ6=sQuery(id+"F0.wireOp",EDGE,"E1.bottom");var subQ7=sQuery(id+"F0.wireOp",EDGE,"E1.right");var subQ8=sQuery(id+"F0.wireOp",EDGE,"E1.top");var subQ9=sQuery(id+"F0.wireOp",EDGE,"E1.left");var subQ10=sQuery(id+"F0.wireOp",EDGE,"E23.filletArc");var subQ11=sQuery(id+"F0.wireOp",EDGE,"E24.filletArc");Q0=makeQuery(id+"F2.boolean.opBoolean","SPLIT",FACE,{"disambiguationData":[TD([makeQuery(id+"F1.opExtrude","SWEPT_FACE",FACE,{"disambiguationData":[OSD([subQ6])]})])],"derivedFrom":makeQuery(id+"F1.opExtrude","CAP_FACE",FACE,{"disambiguationData":[OSD([subQ6,subQ8,subQ9,subQ7,subQ4,subQ3,subQ2,subQ1,subQ0,subQ5,subQ10,subQ11])],"isStart":true})});}
            var sketch = newSketch(context, id + "F16", { "sketchPlane" : qUnion([Q0])});
            skLineSegment(sketch, "E79", {"start": v(-15, 108) * mm, "end": v(-15, 120) * mm});
            skLineSegment(sketch, "E80", {"start": v(15, 108) * mm, "end": v(15, 120) * mm});
            skArc(sketch, "E81", {"start": v(15, 120) * mm, "mid": v(0, 135) * mm, "end": v(-15, 120) * mm});
            skCircle(sketch, "E82", {"center": v(0, 120) * mm, "radius": 6 * mm});
            skLineSegment(sketch, "E83.0", {"start": v(-70, 90) * mm, "end": v(70, 90) * mm});
            skArc(sketch, "E83.1", {"start": v(-70, 90) * mm, "mid": v(-77.07, 87.07) * mm, "end": v(-80, 80) * mm});
            skLineSegment(sketch, "E83.2", {"start": v(-80, -80) * mm, "end": v(-80, 80) * mm});
            skCircle(sketch, "E83.3", {"center": v(-60, 67.5) * mm, "radius": 4 * mm});
            skArc(sketch, "E83.4", {"start": v(56.15, 48.18) * mm, "mid": v(0, 67.5) * mm, "end": v(-56.15, 48.18) * mm});
            skCircle(sketch, "E83.5", {"center": v(60, 67.5) * mm, "radius": 4 * mm});
            skArc(sketch, "E83.6", {"start": v(80, 80) * mm, "mid": v(77.07, 87.07) * mm, "end": v(70, 90) * mm});
            skLineSegment(sketch, "E83.7", {"start": v(80, -80) * mm, "end": v(80, 80) * mm});
            skLineSegment(sketch, "E83.8", {"start": v(60, 40.3) * mm, "end": v(60, -40.3) * mm});
            skArc(sketch, "E83.9", {"start": v(60, 40.3) * mm, "mid": v(58.99, 44.68) * mm, "end": v(56.15, 48.18) * mm});
            skArc(sketch, "E83.10", {"start": v(-56.15, 48.18) * mm, "mid": v(-58.99, 44.68) * mm, "end": v(-60, 40.3) * mm});
            skLineSegment(sketch, "E83.11", {"start": v(-60, 40.3) * mm, "end": v(-60, -40.3) * mm});
            skArc(sketch, "E83.12", {"start": v(-60, -40.3) * mm, "mid": v(-58.99, -44.68) * mm, "end": v(-56.15, -48.18) * mm});
            skArc(sketch, "E83.13", {"start": v(-56.15, -48.18) * mm, "mid": v(0, -67.5) * mm, "end": v(56.15, -48.18) * mm});
            skArc(sketch, "E83.14", {"start": v(56.15, -48.18) * mm, "mid": v(58.99, -44.68) * mm, "end": v(60, -40.3) * mm});
            skCircle(sketch, "E83.15", {"center": v(60, -67.5) * mm, "radius": 4 * mm});
            skArc(sketch, "E83.16", {"start": v(70, -90) * mm, "mid": v(77.07, -87.07) * mm, "end": v(80, -80) * mm});
            skLineSegment(sketch, "E83.17", {"start": v(-70, -90) * mm, "end": v(70, -90) * mm});
            skArc(sketch, "E83.18", {"start": v(-80, -80) * mm, "mid": v(-77.07, -87.07) * mm, "end": v(-70, -90) * mm});
            skCircle(sketch, "E83.19", {"center": v(-60, -67.5) * mm, "radius": 4 * mm});
            skLineSegment(sketch, "E84", {"start": v(-15, 108) * mm, "end": v(-33, 90) * mm});
            skLineSegment(sketch, "E85", {"start": v(15, 108) * mm, "end": v(33, 90) * mm});
            skLineSegment(sketch, "E86", {"start": v(0, 90) * mm, "end": v(0, 120) * mm, "construction": true});
            skLineSegment(sketch, "E87", {"start": v(-80, 0) * mm, "end": v(80, 0) * mm, "construction": true});
            skArc(sketch, "E88.MirrorCS", {"start": v(15, -120) * mm, "mid": v(0, -135) * mm, "end": v(-15, -120) * mm});
            skLineSegment(sketch, "E89.MirrorCS", {"start": v(-15, -108) * mm, "end": v(-15, -120) * mm});
            skLineSegment(sketch, "E90.MirrorCS", {"start": v(15, -108) * mm, "end": v(15, -120) * mm});
            skLineSegment(sketch, "E91.MirrorCS", {"start": v(15, -108) * mm, "end": v(33, -90) * mm});
            skLineSegment(sketch, "E92.MirrorCS", {"start": v(-15, -108) * mm, "end": v(-33, -90) * mm});
            skCircle(sketch, "E93.MirrorC", {"center": v(0, -120) * mm, "radius": 6 * mm});
            skLineSegment(sketch, "E94.MirrorCS", {"start": v(0, -90) * mm, "end": v(0, -120) * mm, "construction": true});
            skSolve(sketch);
        }
        {
            var Q0;
            Q0=makeQuery(id+"F16.imprint","IMPRINT",FACE,{"disambiguationData":[TD([[makeQuery(id+"F16.imprint","IMPRINT",EDGE,{"derivedFrom":sQuery(id+"F16.wireOp",EDGE,"E79")}),-1.0]])]});
            var Q1;
            {var subQ5=sQuery(id+"F16.wireOp",EDGE,"E83.1");Q1=makeQuery(id+"F16.imprint","IMPRINT",FACE,{"disambiguationData":[TD([[makeQuery(id+"F16.imprint","IMPRINT",EDGE,{"derivedFrom":subQ5}),1.0]])]});}
            var Q2;
            Q2=makeQuery(id+"F16.imprint","IMPRINT",FACE,{"disambiguationData":[TD([[makeQuery(id+"F16.imprint","IMPRINT",EDGE,{"derivedFrom":sQuery(id+"F16.wireOp",EDGE,"E88.MirrorCS")}),-1.0]])]});
            var Q3;
            Q3=makeQuery(id+"F2.opExtrude","CAP_FACE",FACE,{"disambiguationData":[OSD([sQuery(id+"F0.wireOp",EDGE,"E12"),sQuery(id+"F0.wireOp",EDGE,"E13"),sQuery(id+"F0.wireOp",EDGE,"E14"),sQuery(id+"F0.wireOp",EDGE,"E15"),sQuery(id+"F0.wireOp",EDGE,"E17.filletArc"),sQuery(id+"F0.wireOp",EDGE,"E18.filletArc"),sQuery(id+"F0.wireOp",EDGE,"E19.filletArc"),sQuery(id+"F0.wireOp",EDGE,"E20.filletArc"),sQuery(id+"F0.wireOp",EDGE,"E25.0"),sQuery(id+"F0.wireOp",EDGE,"E25.1"),sQuery(id+"F0.wireOp",EDGE,"E25.2"),sQuery(id+"F0.wireOp",EDGE,"E25.3"),sQuery(id+"F0.wireOp",EDGE,"E25.4"),sQuery(id+"F0.wireOp",EDGE,"E25.5"),sQuery(id+"F0.wireOp",EDGE,"E25.6"),sQuery(id+"F0.wireOp",EDGE,"E25.7")])],"isStart":false});
            extrude(context, id + "F17", {"entities" : qUnion([Q0, Q1, Q2]), "endBound" : BoundingType.UP_TO_SURFACE, "depth" : 25 * mm, "endBoundEntityFace" : qUnion([Q3]), "offsetDistance" : 25 * mm});
        }
    });
